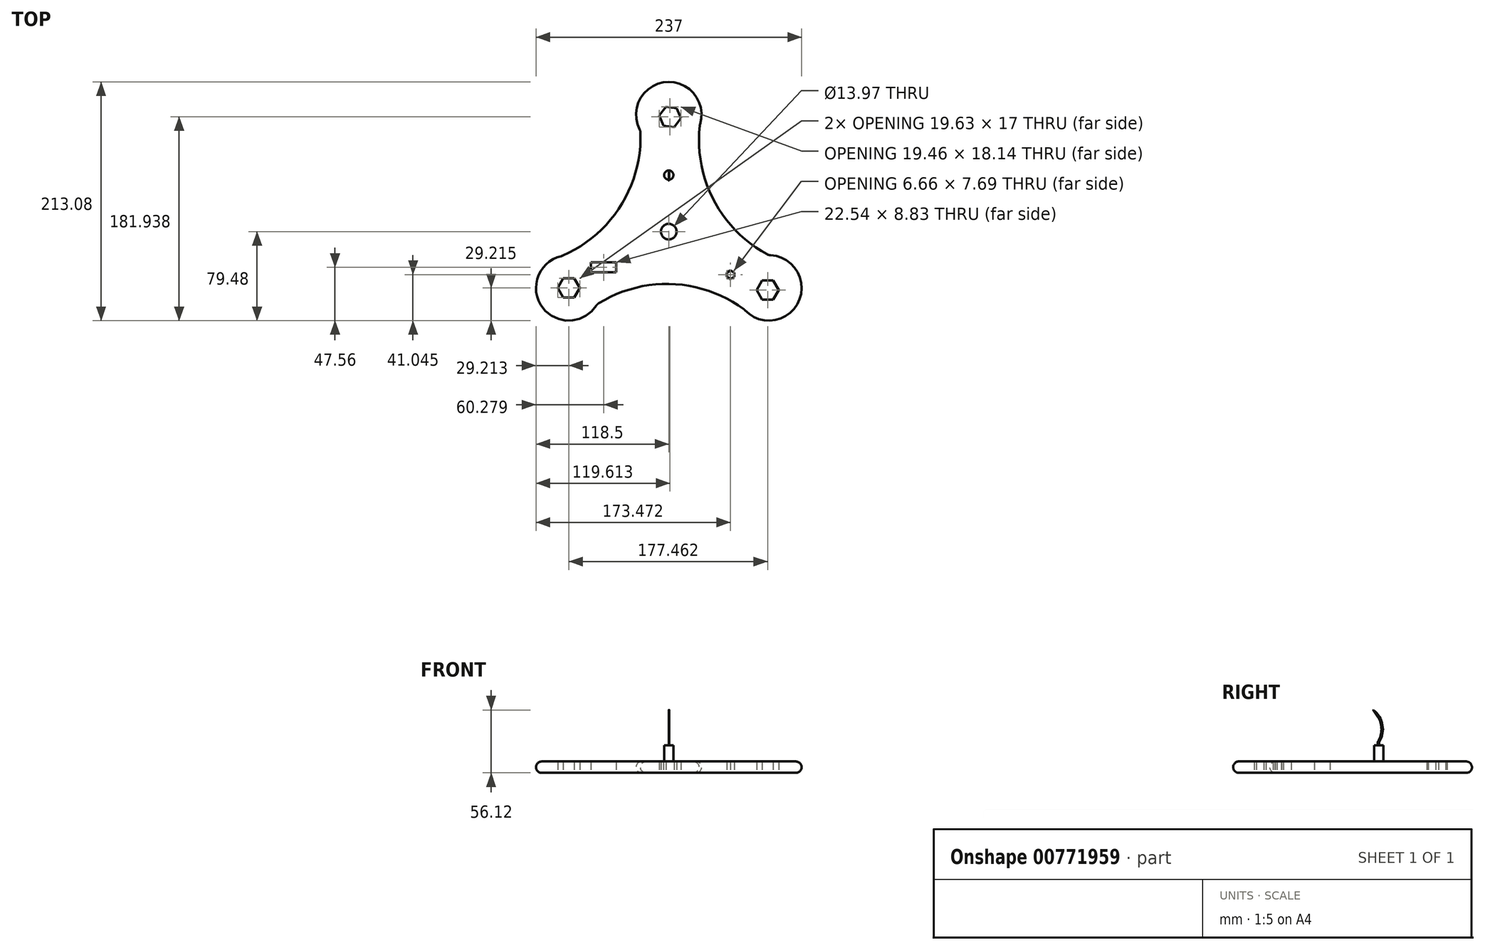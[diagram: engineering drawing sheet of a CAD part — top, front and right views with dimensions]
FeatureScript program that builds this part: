
annotation { "Feature Type Name" : "Feature", "Feature Type Description" : "" }
export const myFeature = defineFeature(function(context is Context, id is Id, definition is map)
    precondition{}
    {
        {
            var Q0;
            Q0=qCreatedBy(makeId("Top.planeOp"),FACE);
            var sketch = newSketch(context, id + "F0", { "sketchPlane" : qUnion([Q0])});
            skCircle(sketch, "E0", {"center": v(0, 0) * mm, "radius": 6.99 * mm});
            skArc(sketch, "E1", {"start": v(27.76, 95.28) * mm, "mid": v(-3.01, 133.44) * mm, "end": v(-25.3, 89.78) * mm});
            skPoint(sketch, "E2.center.orphan", {"position": v(87.86, -42.04) * mm});
            skPoint(sketch, "E3.center.orphan", {"position": v(-75.14, -42.04) * mm});
            skArc(sketch, "E4.1.0", {"start": v(-95.28, -21.68) * mm, "mid": v(-112.94, -67.4) * mm, "end": v(-64, -64.87) * mm});
            skCircle(sketch, "E4.1.1", {"center": v(-89.29, -50.26) * mm, "radius": 8.5 * mm});
            skArc(sketch, "E4.2.0", {"start": v(67.53, -69.75) * mm, "mid": v(115.96, -62.18) * mm, "end": v(89.29, -21.06) * mm});
            skPoint(sketch, "E4.center", {"position": v(0, 1.29) * mm});
            skArc(sketch, "E5", {"start": v(29.2, 104.38) * mm, "mid": v(38.3, 31.63) * mm, "end": v(89.29, -21.06) * mm});
            skArc(sketch, "E6.1.0", {"start": v(-103.9, -24.97) * mm, "mid": v(-45.42, 19.27) * mm, "end": v(-25.3, 89.78) * mm});
            skArc(sketch, "E6.2.0", {"start": v(74.68, -75.56) * mm, "mid": v(7.13, -47.05) * mm, "end": v(-64, -64.87) * mm});
            skCircle(sketch, "E7.1.0", {"center": v(88.17, -52.2) * mm, "radius": 8.5 * mm});
            skCircle(sketch, "E7.2.0", {"center": v(1.11, 102.46) * mm, "radius": 8.5 * mm});
            skCircle(sketch, "E8.cCircle", {"center": v(-89.29, -50.26) * mm, "radius": 8.5 * mm, "construction": true});
            skLineSegment(sketch, "E8.0", {"start": v(-84.38, -58.76) * mm, "end": v(-94.2, -58.76) * mm});
            skLineSegment(sketch, "E8.1", {"start": v(-94.2, -58.76) * mm, "end": v(-99.1, -50.26) * mm});
            skLineSegment(sketch, "E8.2", {"start": v(-99.1, -50.26) * mm, "end": v(-94.2, -41.76) * mm});
            skLineSegment(sketch, "E8.3", {"start": v(-94.2, -41.76) * mm, "end": v(-84.38, -41.76) * mm});
            skLineSegment(sketch, "E8.4", {"start": v(-84.38, -41.76) * mm, "end": v(-79.47, -50.26) * mm});
            skLineSegment(sketch, "E8.5", {"start": v(-79.47, -50.26) * mm, "end": v(-84.38, -58.76) * mm});
            skPoint(sketch, "E8.0.midPoint", {"position": v(-89.29, -58.76) * mm});
            skCircle(sketch, "E9.cCircle", {"center": v(88.17, -52.2) * mm, "radius": 8.5 * mm, "construction": true});
            skLineSegment(sketch, "E9.0", {"start": v(93.08, -60.7) * mm, "end": v(83.27, -60.7) * mm});
            skLineSegment(sketch, "E9.1", {"start": v(83.27, -60.7) * mm, "end": v(78.36, -52.2) * mm});
            skLineSegment(sketch, "E9.2", {"start": v(78.36, -52.2) * mm, "end": v(83.27, -43.7) * mm});
            skLineSegment(sketch, "E9.3", {"start": v(83.27, -43.7) * mm, "end": v(93.08, -43.7) * mm});
            skLineSegment(sketch, "E9.4", {"start": v(93.08, -43.7) * mm, "end": v(97.99, -52.2) * mm});
            skLineSegment(sketch, "E9.5", {"start": v(97.99, -52.2) * mm, "end": v(93.08, -60.7) * mm});
            skPoint(sketch, "E9.0.midPoint", {"position": v(88.17, -60.7) * mm});
            skCircle(sketch, "E10.cCircle", {"center": v(1.11, 102.46) * mm, "radius": 8.5 * mm, "construction": true});
            skLineSegment(sketch, "E10.0", {"start": v(4.87, 93.39) * mm, "end": v(-4.87, 94.67) * mm});
            skLineSegment(sketch, "E10.1", {"start": v(-4.87, 94.67) * mm, "end": v(-8.62, 103.74) * mm});
            skLineSegment(sketch, "E10.2", {"start": v(-8.62, 103.74) * mm, "end": v(-2.64, 111.53) * mm});
            skLineSegment(sketch, "E10.3", {"start": v(-2.64, 111.53) * mm, "end": v(7.1, 110.24) * mm});
            skLineSegment(sketch, "E10.4", {"start": v(7.1, 110.24) * mm, "end": v(10.84, 101.17) * mm});
            skLineSegment(sketch, "E10.5", {"start": v(10.84, 101.17) * mm, "end": v(4.87, 93.39) * mm});
            skPoint(sketch, "E10.0.midPoint", {"position": v(0, 94.03) * mm});
            skCircle(sketch, "E11", {"center": v(54.97, -38.43) * mm, "radius": 3.33 * mm});
            skCircle(sketch, "E12.cCircle", {"center": v(54.97, -38.43) * mm, "radius": 3.33 * mm, "construction": true});
            skLineSegment(sketch, "E12.0", {"start": v(58.3, -36.51) * mm, "end": v(58.3, -40.36) * mm});
            skLineSegment(sketch, "E12.1", {"start": v(58.3, -40.36) * mm, "end": v(54.97, -42.28) * mm});
            skLineSegment(sketch, "E12.2", {"start": v(54.97, -42.28) * mm, "end": v(51.64, -40.36) * mm});
            skLineSegment(sketch, "E12.3", {"start": v(51.64, -40.36) * mm, "end": v(51.64, -36.51) * mm});
            skLineSegment(sketch, "E12.4", {"start": v(51.64, -36.51) * mm, "end": v(54.97, -34.59) * mm});
            skLineSegment(sketch, "E12.5", {"start": v(54.97, -34.59) * mm, "end": v(58.3, -36.51) * mm});
            skPoint(sketch, "E12.0.midPoint", {"position": v(58.3, -38.43) * mm});
            skCircle(sketch, "E13", {"center": v(0, 50.45) * mm, "radius": 4.13 * mm});
            skLineSegment(sketch, "E14.bottom", {"start": v(-69.5, -27.5) * mm, "end": v(-46.95, -27.5) * mm});
            skLineSegment(sketch, "E14.top", {"start": v(-69.5, -36.33) * mm, "end": v(-46.95, -36.33) * mm});
            skLineSegment(sketch, "E14.left", {"start": v(-69.5, -27.5) * mm, "end": v(-69.5, -36.33) * mm});
            skLineSegment(sketch, "E14.right", {"start": v(-46.95, -27.5) * mm, "end": v(-46.95, -36.33) * mm});
            skPoint(sketch, "E14.middle", {"position": v(-58.22, -31.92) * mm});
            skSolve(sketch);
        }
        {
            var Q0;
            Q0=qSketchRegion(id+"F0",true);
            extrude(context, id + "F1", {"entities" : qUnion([Q0]), "depth" : 10.16 * mm, "offsetDistance" : 25.4 * mm});
        }
        {
            var Q0;
            Q0=makeQuery(id+"F1.opExtrude","SWEPT_EDGE",EDGE,{"disambiguationData":[OSD([sQuery(id+"F0.wireOp",EDGE,"E1"),sQuery(id+"F0.wireOp",EDGE,"E5")])]});
            var Q1;
            Q1=makeQuery(id+"F1.opExtrude","SWEPT_EDGE",EDGE,{"disambiguationData":[OSD([sQuery(id+"F0.wireOp",EDGE,"E1"),sQuery(id+"F0.wireOp",EDGE,"E6.1.0")])]});
            var Q2;
            Q2=makeQuery(id+"F1.opExtrude","SWEPT_EDGE",EDGE,{"disambiguationData":[OSD([sQuery(id+"F0.wireOp",EDGE,"E4.1.0"),sQuery(id+"F0.wireOp",EDGE,"E6.2.0")])]});
            var Q3;
            Q3=makeQuery(id+"F1.opExtrude","SWEPT_EDGE",EDGE,{"disambiguationData":[OSD([sQuery(id+"F0.wireOp",EDGE,"E4.1.0"),sQuery(id+"F0.wireOp",EDGE,"E6.1.0")])]});
            var Q4;
            Q4=makeQuery(id+"F1.opExtrude","SWEPT_EDGE",EDGE,{"disambiguationData":[OSD([sQuery(id+"F0.wireOp",EDGE,"E4.2.0"),sQuery(id+"F0.wireOp",EDGE,"E6.2.0")])]});
            var Q5;
            Q5=makeQuery(id+"F1.opExtrude","SWEPT_EDGE",EDGE,{"disambiguationData":[OSD([sQuery(id+"F0.wireOp",EDGE,"E4.2.0"),sQuery(id+"F0.wireOp",EDGE,"E5")])]});
            fillet(context, id + "F2", {"entities" : qUnion([Q0, Q1, Q2, Q3, Q4, Q5]), "radius" : 7.62 * mm, "tangentPropagation" : true, "allowEdgeOverflow" : false});
        }
        {
            var Q0;
            Q0=makeQuery(id+"F0.imprint","IMPRINT",FACE,{"disambiguationData":[TD([[makeQuery(id+"F0.imprint","IMPRINT",EDGE,{"derivedFrom":sQuery(id+"F0.wireOp",EDGE,"E13")}),1.0]])]});
            extrude(context, id + "F3", {"entities" : qUnion([Q0]), "operationType" : NewBodyOperationType.ADD, "depth" : 24.4 * mm, "offsetDistance" : 25.4 * mm});
        }
        {
            var Q0;
            Q0=qCreatedBy(makeId("Right.planeOp"),FACE);
            var sketch = newSketch(context, id + "F4", { "sketchPlane" : qUnion([Q0])});
            skPoint(sketch, "E15", {"position": v(49.6, 24.38) * mm});
            skLineSegment(sketch, "E16", {"start": v(49.6, 24.38) * mm, "end": v(49.6, 27.82) * mm});
            skArc(sketch, "E17", {"start": v(49.6, 27.82) * mm, "mid": v(52.89, 38.92) * mm, "end": v(49.6, 50.03) * mm});
            skArc(sketch, "E18.0", {"start": v(50.87, 27.45) * mm, "mid": v(53.8, 42.84) * mm, "end": v(45.6, 56.17) * mm});
            skLineSegment(sketch, "E18.1", {"start": v(50.87, 24.38) * mm, "end": v(50.87, 27.45) * mm});
            skLineSegment(sketch, "E19", {"start": v(49.6, 50.03) * mm, "end": v(45.6, 55.56) * mm});
            skLineSegment(sketch, "E20", {"start": v(49.6, 24.38) * mm, "end": v(50.87, 24.38) * mm});
            skLineSegment(sketch, "E21", {"start": v(45.6, 56.17) * mm, "end": v(45.6, 55.56) * mm});
            skSolve(sketch);
        }
        {
            var Q0;
            Q0=makeQuery(id+"F4.imprint","IMPRINT",FACE,{"disambiguationData":[TD([[makeQuery(id+"F4.imprint","IMPRINT",EDGE,{"derivedFrom":sQuery(id+"F4.wireOp",EDGE,"E16")}),-1.0]])]});
            extrude(context, id + "F5", {"entities" : qUnion([Q0]), "operationType" : NewBodyOperationType.ADD, "depth" : 0.5 * mm, "offsetDistance" : 25.4 * mm});
        }
        {
            var Q0;
            Q0=makeQuery(id+"F5.opExtrude","CAP_EDGE",EDGE,{"disambiguationData":[OSD([sQuery(id+"F4.wireOp",EDGE,"E18.0")])],"isStart":false});
            var Q1;
            Q1=makeQuery(id+"F5.opExtrude","CAP_EDGE",EDGE,{"disambiguationData":[OSD([sQuery(id+"F4.wireOp",EDGE,"E19")])],"isStart":false});
            var Q2;
            Q2=makeQuery(id+"F5.opExtrude","SWEPT_EDGE",EDGE,{"disambiguationData":[OSD([sQuery(id+"F4.wireOp",EDGE,"E18.0"),sQuery(id+"F4.wireOp",EDGE,"E19")])]});
            var Q3;
            Q3=makeQuery(id+"F5.opExtrude","CAP_EDGE",EDGE,{"disambiguationData":[OSD([sQuery(id+"F4.wireOp",EDGE,"E19")])],"isStart":true});
            var Q4;
            Q4=makeQuery(id+"F5.opExtrude","SWEPT_EDGE",EDGE,{"disambiguationData":[OSD([sQuery(id+"F4.wireOp",EDGE,"E17"),sQuery(id+"F4.wireOp",EDGE,"E19")])]});
            var Q5;
            Q5=makeQuery(id+"F5.opExtrude","CAP_EDGE",EDGE,{"disambiguationData":[OSD([sQuery(id+"F4.wireOp",EDGE,"E17")])],"isStart":false});
            var Q6;
            Q6=makeQuery(id+"F5.opExtrude","SWEPT_EDGE",EDGE,{"disambiguationData":[OSD([sQuery(id+"F4.wireOp",EDGE,"E16"),sQuery(id+"F4.wireOp",EDGE,"E17")])]});
            fillet(context, id + "F6", {"entities" : qUnion([Q0, Q1, Q2, Q3, Q4, Q5, Q6]), "radius" : 0.05 * mm, "tangentPropagation" : true, "allowEdgeOverflow" : false});
        }
        {
            var Q0;
            Q0=makeQuery(id+"F1.opExtrude","SWEPT_FACE",FACE,{"disambiguationData":[OSD([sQuery(id+"F0.wireOp",EDGE,"E4.1.0")])]});
            fillet(context, id + "F7", {"entities" : qUnion([Q0]), "radius" : 5.08 * mm, "tangentPropagation" : true, "allowEdgeOverflow" : false});
        }
    });
